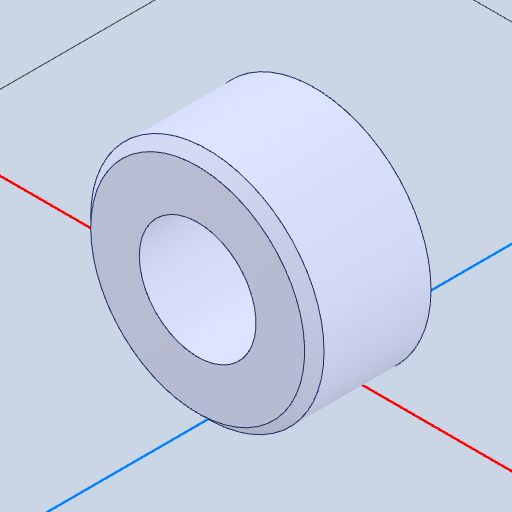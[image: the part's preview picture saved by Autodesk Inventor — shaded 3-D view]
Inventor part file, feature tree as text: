
AUTODESK INVENTOR PART (.ipt)
format: ipt  version: 2022 (Build 260153000, 153)  size: 113,152 bytes
history: native  units: mm
features: other x1, chamfer x1
ambient origin geometry x8: Origin, YZ Plane, XZ Plane, XY Plane, X Axis, Y Axis, Z Axis, Center Point
bodies: Body1 (feature_tree)
feature tree (2):
  other  "Твердое тело1"
  chamfer  "Chamfer1"  [1 undecoded]
note: 1 required parameter value undecoded (feature->parameter linkage not recoverable at this tier; creation-order binding heuristic only, values carry confidence <= 0.55)
